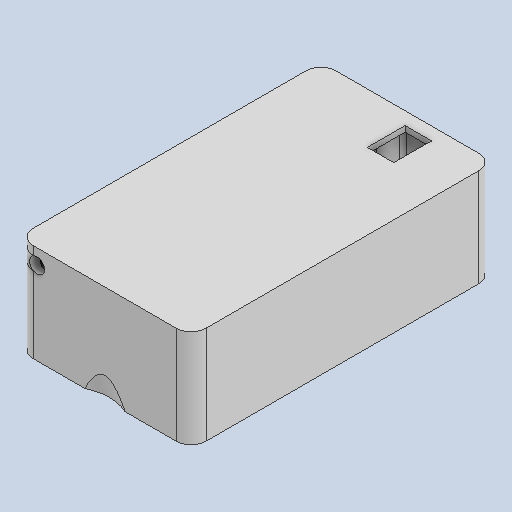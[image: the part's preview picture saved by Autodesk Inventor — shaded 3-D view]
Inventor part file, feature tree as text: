
AUTODESK INVENTOR PART (.ipt)
format: ipt  version: 2022 (Build 260153000, 153)  size: 361,984 bytes
history: native  units: mm
features: other x2, shell x1
ambient origin geometry x8: Origin, YZ Plane, XZ Plane, XY Plane, X Axis, Y Axis, Z Axis, Center Point
bodies: Solid1 (feature_tree)
feature tree (3):
  other  "atTiny85 board.ipt"
  shell  "Shell::atTiny85 board.ipt"  Thickness=10.0mm
  other  "TaggingFeature1"
